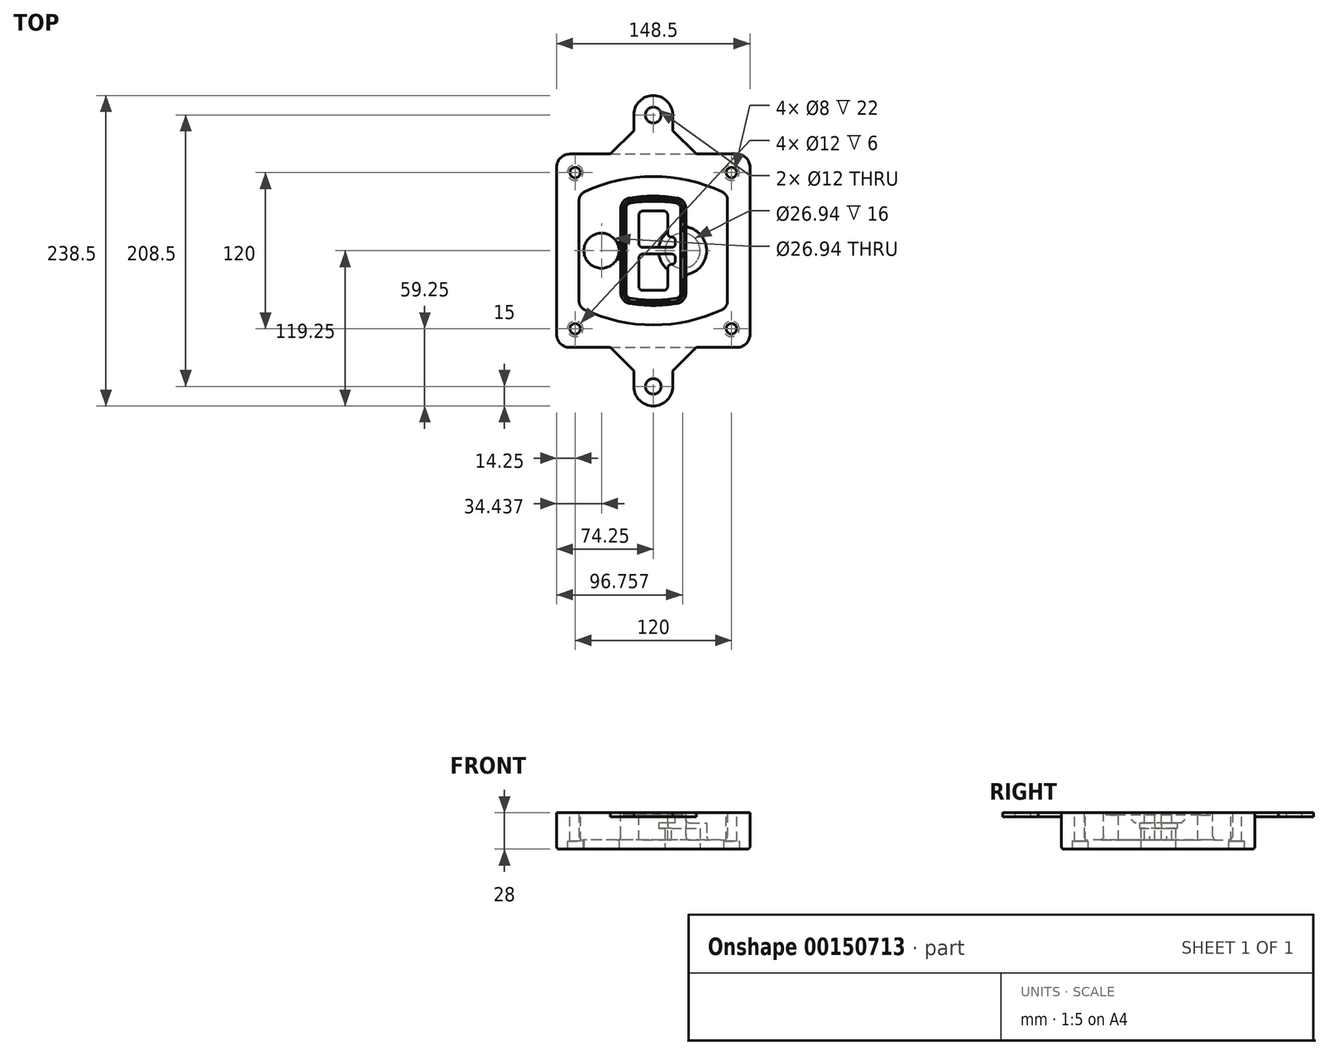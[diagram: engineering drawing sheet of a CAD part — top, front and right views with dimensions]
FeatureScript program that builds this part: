
annotation { "Feature Type Name" : "Feature", "Feature Type Description" : "" }
export const myFeature = defineFeature(function(context is Context, id is Id, definition is map)
    precondition{}
    {
        {
            var Q0;
            Q0=qCreatedBy(makeId("Top.planeOp"),FACE);
            var sketch = newSketch(context, id + "F0", { "sketchPlane" : qUnion([Q0])});
            skPoint(sketch, "E0.rect.middle", {"position": v(0, 0) * mm});
            skLineSegment(sketch, "E1.bottom", {"start": v(-64.25, -74.25) * mm, "end": v(64.25, -74.25) * mm});
            skLineSegment(sketch, "E1.top", {"start": v(-64.25, 74.25) * mm, "end": v(64.25, 74.25) * mm});
            skLineSegment(sketch, "E1.left", {"start": v(-74.25, -64.25) * mm, "end": v(-74.25, 64.25) * mm});
            skLineSegment(sketch, "E1.right", {"start": v(74.25, -64.25) * mm, "end": v(74.25, 64.25) * mm});
            skLineSegment(sketch, "E2", {"start": v(-74.25, 74.25) * mm, "end": v(74.25, -74.25) * mm, "construction": true});
            skLineSegment(sketch, "E3", {"start": v(74.25, 74.25) * mm, "end": v(-74.25, -74.25) * mm, "construction": true});
            skCircle(sketch, "E4", {"center": v(-60, 60) * mm, "radius": 4 * mm});
            skCircle(sketch, "E5", {"center": v(60, 60) * mm, "radius": 4 * mm});
            skCircle(sketch, "E6", {"center": v(60, -60) * mm, "radius": 4 * mm});
            skCircle(sketch, "E7", {"center": v(-60, -60) * mm, "radius": 4 * mm});
            skLineSegment(sketch, "E8", {"start": v(-60, 60) * mm, "end": v(60, 60) * mm, "construction": true});
            skLineSegment(sketch, "E9", {"start": v(60, 60) * mm, "end": v(60, -60) * mm, "construction": true});
            skLineSegment(sketch, "E10", {"start": v(60, -60) * mm, "end": v(-60, -60) * mm, "construction": true});
            skLineSegment(sketch, "E11", {"start": v(-60, -60) * mm, "end": v(-60, 60) * mm, "construction": true});
            skLineSegment(sketch, "E12", {"start": v(-60, 38.83) * mm, "end": v(-60, -38.83) * mm});
            skLineSegment(sketch, "E13", {"start": v(60, 38.83) * mm, "end": v(60, -38.83) * mm});
            skArc(sketch, "E14", {"start": v(54.26, 47.88) * mm, "mid": v(0, 60) * mm, "end": v(-54.26, 47.88) * mm});
            skArc(sketch, "E15", {"start": v(-54.26, -47.88) * mm, "mid": v(0, -60) * mm, "end": v(54.26, -47.88) * mm});
            skLineSegment(sketch, "E16", {"start": v(-60, 0) * mm, "end": v(60, 0) * mm, "construction": true});
            skPoint(sketch, "E17.visualSharp", {"position": v(-60, -45) * mm});
            skArc(sketch, "E17.filletArc", {"start": v(-60, -38.83) * mm, "mid": v(-58.44, -44.2) * mm, "end": v(-54.26, -47.88) * mm});
            skPoint(sketch, "E18.visualSharp", {"position": v(-60, 45) * mm});
            skArc(sketch, "E18.filletArc", {"start": v(-54.26, 47.88) * mm, "mid": v(-58.44, 44.2) * mm, "end": v(-60, 38.83) * mm});
            skPoint(sketch, "E19.visualSharp", {"position": v(60, 45) * mm});
            skArc(sketch, "E19.filletArc", {"start": v(60, 38.83) * mm, "mid": v(58.44, 44.2) * mm, "end": v(54.26, 47.88) * mm});
            skPoint(sketch, "E20.visualSharp", {"position": v(60, -45) * mm});
            skArc(sketch, "E20.filletArc", {"start": v(54.26, -47.88) * mm, "mid": v(58.44, -44.2) * mm, "end": v(60, -38.83) * mm});
            skPoint(sketch, "E21.visualSharp", {"position": v(-74.25, 74.25) * mm});
            skArc(sketch, "E21.filletArc", {"start": v(-64.25, 74.25) * mm, "mid": v(-71.32, 71.32) * mm, "end": v(-74.25, 64.25) * mm});
            skPoint(sketch, "E22.visualSharp", {"position": v(74.25, 74.25) * mm});
            skArc(sketch, "E22.filletArc", {"start": v(74.25, 64.25) * mm, "mid": v(71.32, 71.32) * mm, "end": v(64.25, 74.25) * mm});
            skPoint(sketch, "E23.visualSharp", {"position": v(74.25, -74.25) * mm});
            skArc(sketch, "E23.filletArc", {"start": v(64.25, -74.25) * mm, "mid": v(71.32, -71.32) * mm, "end": v(74.25, -64.25) * mm});
            skPoint(sketch, "E24.visualSharp", {"position": v(-74.25, -74.25) * mm});
            skArc(sketch, "E24.filletArc", {"start": v(-74.25, -64.25) * mm, "mid": v(-71.32, -71.32) * mm, "end": v(-64.25, -74.25) * mm});
            skArc(sketch, "E25.0", {"start": v(57, 38.83) * mm, "mid": v(55.9, 42.58) * mm, "end": v(52.98, 45.17) * mm});
            skLineSegment(sketch, "E25.1", {"start": v(57, 38.83) * mm, "end": v(57, -38.83) * mm});
            skArc(sketch, "E25.2", {"start": v(52.98, -45.17) * mm, "mid": v(55.9, -42.58) * mm, "end": v(57, -38.83) * mm});
            skArc(sketch, "E25.3", {"start": v(-52.98, -45.17) * mm, "mid": v(0, -57) * mm, "end": v(52.98, -45.17) * mm});
            skArc(sketch, "E25.4", {"start": v(-57, -38.83) * mm, "mid": v(-55.9, -42.58) * mm, "end": v(-52.98, -45.17) * mm});
            skArc(sketch, "E25.5", {"start": v(52.98, 45.17) * mm, "mid": v(0, 57) * mm, "end": v(-52.98, 45.17) * mm});
            skLineSegment(sketch, "E25.6", {"start": v(-57, 38.83) * mm, "end": v(-57, -38.83) * mm});
            skArc(sketch, "E25.7", {"start": v(-52.98, 45.17) * mm, "mid": v(-55.9, 42.58) * mm, "end": v(-57, 38.83) * mm});
            skArc(sketch, "E26.0", {"start": v(-55.96, 51.5) * mm, "mid": v(-61.82, 46.33) * mm, "end": v(-64, 38.83) * mm});
            skArc(sketch, "E26.1", {"start": v(55.96, 51.5) * mm, "mid": v(0, 64) * mm, "end": v(-55.96, 51.5) * mm});
            skArc(sketch, "E26.2", {"start": v(64, 38.83) * mm, "mid": v(61.82, 46.33) * mm, "end": v(55.96, 51.5) * mm});
            skLineSegment(sketch, "E26.3", {"start": v(64, 38.83) * mm, "end": v(64, -38.83) * mm});
            skArc(sketch, "E26.4", {"start": v(55.96, -51.5) * mm, "mid": v(61.82, -46.33) * mm, "end": v(64, -38.83) * mm});
            skLineSegment(sketch, "E26.5", {"start": v(-64, 38.83) * mm, "end": v(-64, -38.83) * mm});
            skArc(sketch, "E26.6", {"start": v(-55.96, -51.5) * mm, "mid": v(0, -64) * mm, "end": v(55.96, -51.5) * mm});
            skArc(sketch, "E26.7", {"start": v(-64, -38.83) * mm, "mid": v(-61.82, -46.33) * mm, "end": v(-55.96, -51.5) * mm});
            skSolve(sketch);
        }
        {
            var Q0;
            Q0=makeQuery(id+"F0.imprint","IMPRINT",FACE,{"disambiguationData":[TD([[makeQuery(id+"F0.imprint","IMPRINT",EDGE,{"derivedFrom":sQuery(id+"F0.wireOp",EDGE,"E1.bottom")}),1.0]])]});
            var Q1;
            Q1=makeQuery(id+"F0.imprint","IMPRINT",FACE,{"disambiguationData":[TD([[makeQuery(id+"F0.imprint","IMPRINT",EDGE,{"derivedFrom":sQuery(id+"F0.wireOp",EDGE,"E12")}),1.0]])]});
            var Q2;
            Q2=makeQuery(id+"F0.imprint","IMPRINT",FACE,{"disambiguationData":[TD([[makeQuery(id+"F0.imprint","IMPRINT",EDGE,{"derivedFrom":sQuery(id+"F0.wireOp",EDGE,"E25.0")}),1.0]])]});
            var Q3;
            Q3=makeQuery(id+"F0.imprint","IMPRINT",FACE,{"disambiguationData":[TD([[makeQuery(id+"F0.imprint","IMPRINT",EDGE,{"derivedFrom":sQuery(id+"F0.wireOp",EDGE,"E12")}),-1.0]])]});
            extrude(context, id + "F1", {"entities" : qUnion([Q0, Q1, Q2, Q3]), "oppositeDirection" : true, "depth" : 25 * mm});
        }
        {
            var Q0;
            Q0=makeQuery(id+"F0.imprint","IMPRINT",FACE,{"disambiguationData":[TD([[makeQuery(id+"F0.imprint","IMPRINT",EDGE,{"derivedFrom":sQuery(id+"F0.wireOp",EDGE,"E12")}),1.0]])]});
            extrude(context, id + "F2", {"entities" : qUnion([Q0]), "operationType" : NewBodyOperationType.ADD, "depth" : 3 * mm});
        }
        {
            var Q0;
            Q0=makeQuery(id+"F0.imprint","IMPRINT",FACE,{"disambiguationData":[TD([[makeQuery(id+"F0.imprint","IMPRINT",EDGE,{"derivedFrom":sQuery(id+"F0.wireOp",EDGE,"E25.0")}),1.0]])]});
            extrude(context, id + "F3", {"entities" : qUnion([Q0]), "operationType" : NewBodyOperationType.REMOVE, "oppositeDirection" : true, "depth" : 18 * mm});
        }
        {
            var Q0;
            Q0=makeQuery(id+"F2.opExtrude","CAP_FACE",FACE,{"disambiguationData":[OSD([sQuery(id+"F0.wireOp",EDGE,"E12"),sQuery(id+"F0.wireOp",EDGE,"E13"),sQuery(id+"F0.wireOp",EDGE,"E14"),sQuery(id+"F0.wireOp",EDGE,"E15"),sQuery(id+"F0.wireOp",EDGE,"E17.filletArc"),sQuery(id+"F0.wireOp",EDGE,"E18.filletArc"),sQuery(id+"F0.wireOp",EDGE,"E19.filletArc"),sQuery(id+"F0.wireOp",EDGE,"E20.filletArc"),sQuery(id+"F0.wireOp",EDGE,"E25.0"),sQuery(id+"F0.wireOp",EDGE,"E25.1"),sQuery(id+"F0.wireOp",EDGE,"E25.2"),sQuery(id+"F0.wireOp",EDGE,"E25.3"),sQuery(id+"F0.wireOp",EDGE,"E25.4"),sQuery(id+"F0.wireOp",EDGE,"E25.5"),sQuery(id+"F0.wireOp",EDGE,"E25.6"),sQuery(id+"F0.wireOp",EDGE,"E25.7")])],"isStart":false});
            var sketch = newSketch(context, id + "F4", { "sketchPlane" : qUnion([Q0])});
            skArc(sketch, "E27.0", {"start": v(-18.34, -40.45) * mm, "mid": v(0, -42) * mm, "end": v(18.34, -40.45) * mm});
            skArc(sketch, "E28.0", {"start": v(18.34, 40.45) * mm, "mid": v(0, 42) * mm, "end": v(-18.34, 40.45) * mm});
            skLineSegment(sketch, "E29", {"start": v(-25, 32.57) * mm, "end": v(-25, -32.57) * mm});
            skLineSegment(sketch, "E30", {"start": v(25, 32.57) * mm, "end": v(25, -32.57) * mm});
            skLineSegment(sketch, "E31", {"start": v(-25, 39.1) * mm, "end": v(25, 39.1) * mm, "construction": true});
            skLineSegment(sketch, "E32", {"start": v(-25, -39.1) * mm, "end": v(25, -39.1) * mm, "construction": true});
            skPoint(sketch, "E33.visualSharp", {"position": v(-25, 39.1) * mm});
            skArc(sketch, "E33.filletArc", {"start": v(-18.34, 40.45) * mm, "mid": v(-23.11, 37.73) * mm, "end": v(-25, 32.57) * mm});
            skPoint(sketch, "E34.visualSharp", {"position": v(25, 39.1) * mm});
            skArc(sketch, "E34.filletArc", {"start": v(25, 32.57) * mm, "mid": v(23.11, 37.73) * mm, "end": v(18.34, 40.45) * mm});
            skPoint(sketch, "E35.visualSharp", {"position": v(25, -39.1) * mm});
            skArc(sketch, "E35.filletArc", {"start": v(18.34, -40.45) * mm, "mid": v(23.11, -37.73) * mm, "end": v(25, -32.57) * mm});
            skPoint(sketch, "E36.visualSharp", {"position": v(-25, -39.1) * mm});
            skArc(sketch, "E36.filletArc", {"start": v(-25, -32.57) * mm, "mid": v(-23.11, -37.73) * mm, "end": v(-18.34, -40.45) * mm});
            skArc(sketch, "E37.0", {"start": v(52.98, 45.17) * mm, "mid": v(0, 57) * mm, "end": v(-52.98, 45.17) * mm});
            skArc(sketch, "E37.1", {"start": v(-52.98, 45.17) * mm, "mid": v(-55.9, 42.58) * mm, "end": v(-57, 38.83) * mm});
            skLineSegment(sketch, "E37.2", {"start": v(-57, 38.83) * mm, "end": v(-57, -38.83) * mm});
            skArc(sketch, "E37.3", {"start": v(-57, -38.83) * mm, "mid": v(-55.9, -42.58) * mm, "end": v(-52.98, -45.17) * mm});
            skArc(sketch, "E37.4", {"start": v(-52.98, -45.17) * mm, "mid": v(0, -57) * mm, "end": v(52.98, -45.17) * mm});
            skArc(sketch, "E37.5", {"start": v(52.98, -45.17) * mm, "mid": v(55.9, -42.58) * mm, "end": v(57, -38.83) * mm});
            skLineSegment(sketch, "E37.6", {"start": v(57, 38.83) * mm, "end": v(57, -38.83) * mm});
            skArc(sketch, "E37.7", {"start": v(57, 38.83) * mm, "mid": v(55.9, 42.58) * mm, "end": v(52.98, 45.17) * mm});
            skLineSegment(sketch, "E38.0", {"start": v(23, 32.57) * mm, "end": v(23, -32.57) * mm});
            skArc(sketch, "E38.1", {"start": v(18, -38.48) * mm, "mid": v(21.58, -36.44) * mm, "end": v(23, -32.57) * mm});
            skArc(sketch, "E38.2", {"start": v(-18, -38.48) * mm, "mid": v(0, -40) * mm, "end": v(18, -38.48) * mm});
            skArc(sketch, "E38.3", {"start": v(-23, -32.57) * mm, "mid": v(-21.58, -36.44) * mm, "end": v(-18, -38.48) * mm});
            skLineSegment(sketch, "E38.4", {"start": v(-23, 32.57) * mm, "end": v(-23, -32.57) * mm});
            skArc(sketch, "E38.5", {"start": v(23, 32.57) * mm, "mid": v(21.58, 36.44) * mm, "end": v(18, 38.48) * mm});
            skArc(sketch, "E38.6", {"start": v(-18, 38.48) * mm, "mid": v(-21.58, 36.44) * mm, "end": v(-23, 32.57) * mm});
            skArc(sketch, "E38.7", {"start": v(18, 38.48) * mm, "mid": v(0, 40) * mm, "end": v(-18, 38.48) * mm});
            skArc(sketch, "E39.0", {"start": v(21, 32.57) * mm, "mid": v(20.06, 35.15) * mm, "end": v(17.67, 36.5) * mm});
            skLineSegment(sketch, "E39.1", {"start": v(21, 32.57) * mm, "end": v(21, -32.57) * mm});
            skArc(sketch, "E39.2", {"start": v(17.67, -36.5) * mm, "mid": v(20.06, -35.15) * mm, "end": v(21, -32.57) * mm});
            skArc(sketch, "E39.3", {"start": v(-17.67, -36.5) * mm, "mid": v(0, -38) * mm, "end": v(17.67, -36.5) * mm});
            skArc(sketch, "E39.4", {"start": v(-21, -32.57) * mm, "mid": v(-20.06, -35.15) * mm, "end": v(-17.67, -36.5) * mm});
            skArc(sketch, "E39.5", {"start": v(17.67, 36.5) * mm, "mid": v(0, 38) * mm, "end": v(-17.67, 36.5) * mm});
            skLineSegment(sketch, "E39.6", {"start": v(-21, 32.57) * mm, "end": v(-21, -32.57) * mm});
            skArc(sketch, "E39.7", {"start": v(-17.67, 36.5) * mm, "mid": v(-20.06, 35.15) * mm, "end": v(-21, 32.57) * mm});
            skLineSegment(sketch, "E40", {"start": v(-25, 0) * mm, "end": v(25, 0) * mm, "construction": true});
            skLineSegment(sketch, "E41", {"start": v(-11, 5.5) * mm, "end": v(-11, 27.5) * mm});
            skLineSegment(sketch, "E42", {"start": v(-8, 30.5) * mm, "end": v(8, 30.5) * mm});
            skLineSegment(sketch, "E43", {"start": v(11, 27.5) * mm, "end": v(11, 13.5) * mm});
            skLineSegment(sketch, "E44", {"start": v(14, 10.5) * mm, "end": v(14, 10.5) * mm});
            skLineSegment(sketch, "E45", {"start": v(17, 7.5) * mm, "end": v(17, 5.5) * mm});
            skLineSegment(sketch, "E46", {"start": v(14, 2.5) * mm, "end": v(-8, 2.5) * mm});
            skPoint(sketch, "E47.visualSharp", {"position": v(-11, 30.5) * mm});
            skArc(sketch, "E47.filletArc", {"start": v(-8, 30.5) * mm, "mid": v(-10.12, 29.62) * mm, "end": v(-11, 27.5) * mm});
            skPoint(sketch, "E48.visualSharp", {"position": v(11, 30.5) * mm});
            skArc(sketch, "E48.filletArc", {"start": v(11, 27.5) * mm, "mid": v(10.12, 29.62) * mm, "end": v(8, 30.5) * mm});
            skPoint(sketch, "E49.visualSharp", {"position": v(11, 10.5) * mm});
            skArc(sketch, "E49.filletArc", {"start": v(11, 13.5) * mm, "mid": v(11.88, 11.38) * mm, "end": v(14, 10.5) * mm});
            skPoint(sketch, "E50.visualSharp", {"position": v(17, 10.5) * mm});
            skArc(sketch, "E50.filletArc", {"start": v(17, 7.5) * mm, "mid": v(16.12, 9.62) * mm, "end": v(14, 10.5) * mm});
            skPoint(sketch, "E51.visualSharp", {"position": v(17, 2.5) * mm});
            skArc(sketch, "E51.filletArc", {"start": v(14, 2.5) * mm, "mid": v(16.12, 3.38) * mm, "end": v(17, 5.5) * mm});
            skPoint(sketch, "E52.visualSharp", {"position": v(-11, 2.5) * mm});
            skArc(sketch, "E52.filletArc", {"start": v(-11, 5.5) * mm, "mid": v(-10.12, 3.38) * mm, "end": v(-8, 2.5) * mm});
            skLineSegment(sketch, "E53.0.MirrorCS", {"start": v(14, -2.5) * mm, "end": v(-8, -2.5) * mm});
            skArc(sketch, "E54.0.MirrorCS", {"start": v(-11, -5.5) * mm, "mid": v(-10.12, -3.38) * mm, "end": v(-8, -2.5) * mm});
            skLineSegment(sketch, "E55.0.MirrorCS", {"start": v(-11, -5.5) * mm, "end": v(-11, -27.5) * mm});
            skArc(sketch, "E56.0.MirrorCS", {"start": v(-8, -30.5) * mm, "mid": v(-10.12, -29.62) * mm, "end": v(-11, -27.5) * mm});
            skLineSegment(sketch, "E57.0.MirrorCS", {"start": v(-8, -30.5) * mm, "end": v(8, -30.5) * mm});
            skArc(sketch, "E58.0.MirrorCS", {"start": v(11, -27.5) * mm, "mid": v(10.12, -29.62) * mm, "end": v(8, -30.5) * mm});
            skLineSegment(sketch, "E59.0.MirrorCS", {"start": v(11, -27.5) * mm, "end": v(11, -13.5) * mm});
            skArc(sketch, "E60.0.MirrorCS", {"start": v(11, -13.5) * mm, "mid": v(11.88, -11.38) * mm, "end": v(14, -10.5) * mm});
            skArc(sketch, "E61.0.MirrorCS", {"start": v(17, -7.5) * mm, "mid": v(16.12, -9.62) * mm, "end": v(14, -10.5) * mm});
            skLineSegment(sketch, "E62.0.MirrorCS", {"start": v(17, -7.5) * mm, "end": v(17, -5.5) * mm});
            skArc(sketch, "E63.0.MirrorCS", {"start": v(14, -2.5) * mm, "mid": v(16.12, -3.38) * mm, "end": v(17, -5.5) * mm});
            skSolve(sketch);
        }
        {
            var Q0;
            Q0=makeQuery(id+"F4.imprint","IMPRINT",FACE,{"disambiguationData":[TD([[makeQuery(id+"F4.imprint","IMPRINT",EDGE,{"derivedFrom":sQuery(id+"F4.wireOp",EDGE,"E27.0")}),1.0]])]});
            var Q1;
            Q1=makeQuery(id+"F4.imprint","IMPRINT",FACE,{"disambiguationData":[TD([[makeQuery(id+"F4.imprint","IMPRINT",EDGE,{"derivedFrom":sQuery(id+"F4.wireOp",EDGE,"E38.0")}),-1.0]])]});
            var Q2;
            Q2=makeQuery(id+"F4.imprint","IMPRINT",FACE,{"disambiguationData":[TD([[makeQuery(id+"F4.imprint","IMPRINT",EDGE,{"derivedFrom":sQuery(id+"F4.wireOp",EDGE,"E39.0")}),1.0]])]});
            extrude(context, id + "F5", {"entities" : qUnion([Q0, Q1, Q2]), "operationType" : NewBodyOperationType.ADD, "endBound" : BoundingType.UP_TO_NEXT, "oppositeDirection" : true, "depth" : 25 * mm});
        }
        {
            var Q0;
            Q0=makeQuery(id+"F4.imprint","IMPRINT",FACE,{"disambiguationData":[TD([[makeQuery(id+"F4.imprint","IMPRINT",EDGE,{"derivedFrom":sQuery(id+"F4.wireOp",EDGE,"E38.0")}),-1.0]])]});
            extrude(context, id + "F6", {"entities" : qUnion([Q0]), "operationType" : NewBodyOperationType.REMOVE, "oppositeDirection" : true, "depth" : 2 * mm});
        }
        {
            var Q0;
            Q0=makeQuery(id+"F1.opExtrude","CAP_FACE",FACE,{"disambiguationData":[OSD([sQuery(id+"F0.wireOp",EDGE,"E1.bottom"),sQuery(id+"F0.wireOp",EDGE,"E1.top"),sQuery(id+"F0.wireOp",EDGE,"E1.left"),sQuery(id+"F0.wireOp",EDGE,"E1.right"),sQuery(id+"F0.wireOp",EDGE,"E4"),sQuery(id+"F0.wireOp",EDGE,"E5"),sQuery(id+"F0.wireOp",EDGE,"E6"),sQuery(id+"F0.wireOp",EDGE,"E7"),sQuery(id+"F0.wireOp",EDGE,"E21.filletArc"),sQuery(id+"F0.wireOp",EDGE,"E22.filletArc"),sQuery(id+"F0.wireOp",EDGE,"E23.filletArc"),sQuery(id+"F0.wireOp",EDGE,"E24.filletArc")])],"isStart":false});
            var sketch = newSketch(context, id + "F7", { "sketchPlane" : qUnion([Q0])});
            skCircle(sketch, "E64", {"center": v(22.5, 0) * mm, "radius": 13.47 * mm});
            skCircle(sketch, "E65", {"center": v(-39.81, 0) * mm, "radius": 13.47 * mm});
            skLineSegment(sketch, "E66", {"start": v(74.25, 0) * mm, "end": v(-74.25, 0) * mm});
            skCircle(sketch, "E67", {"center": v(22.5, 0) * mm, "radius": 18.47 * mm});
            skCircle(sketch, "E68", {"center": v(60, -60) * mm, "radius": 6 * mm});
            skCircle(sketch, "E69", {"center": v(-60, -60) * mm, "radius": 6 * mm});
            skCircle(sketch, "E70", {"center": v(-60, 60) * mm, "radius": 6 * mm});
            skCircle(sketch, "E71", {"center": v(60, 60) * mm, "radius": 6 * mm});
            skSolve(sketch);
        }
        {
            var Q0;
            {var subQ1=sQuery(id+"F7.wireOp",EDGE,"E66");var subQ4=sQuery(id+"F7.wireOp",EDGE,"E64");var subQ6=makeQuery(id+"F7.imprint","INTERSECT",VERTEX,{"disambiguationData":[OD(0.0)],"derivedFrom":[subQ4,subQ1]});Q0=makeQuery(id+"F7.imprint","IMPRINT",FACE,{"disambiguationData":[TD([[makeQuery(id+"F7.imprint","IMPRINT",EDGE,{"disambiguationData":[TD([[subQ6,-1.0]])],"derivedFrom":subQ4}),-1.0]])]});}
            var Q1;
            {var subQ0=sQuery(id+"F7.wireOp",EDGE,"E66");var subQ1=sQuery(id+"F7.wireOp",EDGE,"E64");var subQ3=makeQuery(id+"F7.imprint","INTERSECT",VERTEX,{"disambiguationData":[OD(0.0)],"derivedFrom":[subQ1,subQ0]});Q1=makeQuery(id+"F7.imprint","IMPRINT",FACE,{"disambiguationData":[TD([[makeQuery(id+"F7.imprint","IMPRINT",EDGE,{"disambiguationData":[TD([[subQ3,-1.0]])],"derivedFrom":subQ1}),1.0]])]});}
            var Q2;
            {var subQ0=sQuery(id+"F7.wireOp",EDGE,"E66");var subQ1=sQuery(id+"F7.wireOp",EDGE,"E64");var subQ3=makeQuery(id+"F7.imprint","INTERSECT",VERTEX,{"disambiguationData":[OD(0.0)],"derivedFrom":[subQ1,subQ0]});Q2=makeQuery(id+"F7.imprint","IMPRINT",FACE,{"disambiguationData":[TD([[makeQuery(id+"F7.imprint","IMPRINT",EDGE,{"disambiguationData":[TD([[subQ3,1.0]])],"derivedFrom":subQ1}),1.0]])]});}
            var Q3;
            {var subQ1=sQuery(id+"F7.wireOp",EDGE,"E66");var subQ4=sQuery(id+"F7.wireOp",EDGE,"E64");var subQ6=makeQuery(id+"F7.imprint","INTERSECT",VERTEX,{"disambiguationData":[OD(0.0)],"derivedFrom":[subQ4,subQ1]});Q3=makeQuery(id+"F7.imprint","IMPRINT",FACE,{"disambiguationData":[TD([[makeQuery(id+"F7.imprint","IMPRINT",EDGE,{"disambiguationData":[TD([[subQ6,1.0]])],"derivedFrom":subQ4}),-1.0]])]});}
            extrude(context, id + "F8", {"entities" : qUnion([Q0, Q1, Q2, Q3]), "operationType" : NewBodyOperationType.ADD, "oppositeDirection" : true, "depth" : 20 * mm});
        }
        {
            var Q0;
            {var subQ0=sQuery(id+"F7.wireOp",EDGE,"E66");var subQ1=sQuery(id+"F7.wireOp",EDGE,"E64");var subQ3=makeQuery(id+"F7.imprint","INTERSECT",VERTEX,{"disambiguationData":[OD(0.0)],"derivedFrom":[subQ1,subQ0]});Q0=makeQuery(id+"F7.imprint","IMPRINT",FACE,{"disambiguationData":[TD([[makeQuery(id+"F7.imprint","IMPRINT",EDGE,{"disambiguationData":[TD([[subQ3,-1.0]])],"derivedFrom":subQ1}),1.0]])]});}
            var Q1;
            {var subQ0=sQuery(id+"F7.wireOp",EDGE,"E66");var subQ1=sQuery(id+"F7.wireOp",EDGE,"E64");var subQ3=makeQuery(id+"F7.imprint","INTERSECT",VERTEX,{"disambiguationData":[OD(0.0)],"derivedFrom":[subQ1,subQ0]});Q1=makeQuery(id+"F7.imprint","IMPRINT",FACE,{"disambiguationData":[TD([[makeQuery(id+"F7.imprint","IMPRINT",EDGE,{"disambiguationData":[TD([[subQ3,1.0]])],"derivedFrom":subQ1}),1.0]])]});}
            extrude(context, id + "F9", {"entities" : qUnion([Q0, Q1]), "operationType" : NewBodyOperationType.REMOVE, "oppositeDirection" : true, "depth" : 16 * mm});
        }
        {
            var Q0;
            {var subQ0=sQuery(id+"F7.wireOp",EDGE,"E66");var subQ1=sQuery(id+"F7.wireOp",EDGE,"E65");var subQ3=makeQuery(id+"F7.imprint","INTERSECT",VERTEX,{"disambiguationData":[OD(0.0)],"derivedFrom":[subQ1,subQ0]});Q0=makeQuery(id+"F7.imprint","IMPRINT",FACE,{"disambiguationData":[TD([[makeQuery(id+"F7.imprint","IMPRINT",EDGE,{"disambiguationData":[TD([[subQ3,-1.0]])],"derivedFrom":subQ1}),1.0]])]});}
            var Q1;
            {var subQ0=sQuery(id+"F7.wireOp",EDGE,"E66");var subQ1=sQuery(id+"F7.wireOp",EDGE,"E65");var subQ3=makeQuery(id+"F7.imprint","INTERSECT",VERTEX,{"disambiguationData":[OD(0.0)],"derivedFrom":[subQ1,subQ0]});Q1=makeQuery(id+"F7.imprint","IMPRINT",FACE,{"disambiguationData":[TD([[makeQuery(id+"F7.imprint","IMPRINT",EDGE,{"disambiguationData":[TD([[subQ3,1.0]])],"derivedFrom":subQ1}),1.0]])]});}
            extrude(context, id + "F10", {"entities" : qUnion([Q0, Q1]), "operationType" : NewBodyOperationType.REMOVE, "oppositeDirection" : true, "depth" : 25 * mm});
        }
        {
            var Q0;
            Q0=makeQuery(id+"F7.imprint","IMPRINT",FACE,{"disambiguationData":[TD([[makeQuery(id+"F7.imprint","IMPRINT",EDGE,{"derivedFrom":sQuery(id+"F7.wireOp",EDGE,"E68")}),1.0]])]});
            var Q1;
            Q1=makeQuery(id+"F7.imprint","IMPRINT",FACE,{"disambiguationData":[TD([[makeQuery(id+"F7.imprint","IMPRINT",EDGE,{"derivedFrom":makeQuery(id+"F1.opExtrude","CAP_EDGE",EDGE,{"disambiguationData":[OSD([sQuery(id+"F0.wireOp",EDGE,"E5")])],"isStart":false})}),-1.0]])]});
            var Q2;
            Q2=makeQuery(id+"F7.imprint","IMPRINT",FACE,{"disambiguationData":[TD([[makeQuery(id+"F7.imprint","IMPRINT",EDGE,{"derivedFrom":sQuery(id+"F7.wireOp",EDGE,"E69")}),1.0]])]});
            var Q3;
            Q3=makeQuery(id+"F7.imprint","IMPRINT",FACE,{"disambiguationData":[TD([[makeQuery(id+"F7.imprint","IMPRINT",EDGE,{"derivedFrom":makeQuery(id+"F1.opExtrude","CAP_EDGE",EDGE,{"disambiguationData":[OSD([sQuery(id+"F0.wireOp",EDGE,"E4")])],"isStart":false})}),-1.0]])]});
            var Q4;
            Q4=makeQuery(id+"F7.imprint","IMPRINT",FACE,{"disambiguationData":[TD([[makeQuery(id+"F7.imprint","IMPRINT",EDGE,{"derivedFrom":sQuery(id+"F7.wireOp",EDGE,"E70")}),1.0]])]});
            var Q5;
            Q5=makeQuery(id+"F7.imprint","IMPRINT",FACE,{"disambiguationData":[TD([[makeQuery(id+"F7.imprint","IMPRINT",EDGE,{"derivedFrom":makeQuery(id+"F1.opExtrude","CAP_EDGE",EDGE,{"disambiguationData":[OSD([sQuery(id+"F0.wireOp",EDGE,"E7")])],"isStart":false})}),-1.0]])]});
            var Q6;
            Q6=makeQuery(id+"F7.imprint","IMPRINT",FACE,{"disambiguationData":[TD([[makeQuery(id+"F7.imprint","IMPRINT",EDGE,{"derivedFrom":sQuery(id+"F7.wireOp",EDGE,"E71")}),1.0]])]});
            var Q7;
            Q7=makeQuery(id+"F7.imprint","IMPRINT",FACE,{"disambiguationData":[TD([[makeQuery(id+"F7.imprint","IMPRINT",EDGE,{"derivedFrom":makeQuery(id+"F1.opExtrude","CAP_EDGE",EDGE,{"disambiguationData":[OSD([sQuery(id+"F0.wireOp",EDGE,"E6")])],"isStart":false})}),-1.0]])]});
            extrude(context, id + "F11", {"entities" : qUnion([Q0, Q1, Q2, Q3, Q4, Q5, Q6, Q7]), "operationType" : NewBodyOperationType.REMOVE, "oppositeDirection" : true, "depth" : 6 * mm});
        }
        {
            var Q0;
            Q0=makeQuery(id+"F9.boolean.opBoolean","COPY",FACE,{"derivedFrom":makeQuery(id+"F9.opExtrude","CAP_FACE",FACE,{"disambiguationData":[OSD([sQuery(id+"F7.wireOp",EDGE,"E64")])],"isStart":false})});
            var sketch = newSketch(context, id + "F12", { "sketchPlane" : qUnion([Q0])});
            skArc(sketch, "E72.0", {"start": v(11, 14.45) * mm, "mid": v(6.45, 9.13) * mm, "end": v(4.2, 2.5) * mm});
            skArc(sketch, "E72.1", {"start": v(4.2, -2.5) * mm, "mid": v(6.45, -9.13) * mm, "end": v(11, -14.45) * mm});
            skLineSegment(sketch, "E73", {"start": v(4.2, -2.5) * mm, "end": v(14, -2.5) * mm});
            skLineSegment(sketch, "E74.0", {"start": v(14, 2.5) * mm, "end": v(4.2, 2.5) * mm});
            skArc(sketch, "E74.1", {"start": v(14, 2.5) * mm, "mid": v(16.12, 3.38) * mm, "end": v(17, 5.5) * mm});
            skLineSegment(sketch, "E74.2", {"start": v(17, 7.5) * mm, "end": v(17, 5.5) * mm});
            skArc(sketch, "E74.3", {"start": v(17, 7.5) * mm, "mid": v(16.12, 9.62) * mm, "end": v(14, 10.5) * mm});
            skArc(sketch, "E74.4", {"start": v(11, 13.5) * mm, "mid": v(11.88, 11.38) * mm, "end": v(14, 10.5) * mm});
            skLineSegment(sketch, "E74.5", {"start": v(11, 14.45) * mm, "end": v(11, 13.5) * mm});
            skLineSegment(sketch, "E74.7", {"start": v(14, -2.5) * mm, "end": v(4.2, -2.5) * mm});
            skArc(sketch, "E74.8", {"start": v(14, -2.5) * mm, "mid": v(16.12, -3.38) * mm, "end": v(17, -5.5) * mm});
            skLineSegment(sketch, "E74.9", {"start": v(17, -7.5) * mm, "end": v(17, -5.5) * mm});
            skArc(sketch, "E74.10", {"start": v(17, -7.5) * mm, "mid": v(16.12, -9.62) * mm, "end": v(14, -10.5) * mm});
            skArc(sketch, "E74.11", {"start": v(11, -13.5) * mm, "mid": v(11.88, -11.38) * mm, "end": v(14, -10.5) * mm});
            skLineSegment(sketch, "E74.12", {"start": v(11, -14.45) * mm, "end": v(11, -13.5) * mm});
            skPoint(sketch, "E75.orphan", {"position": v(11, -27.5) * mm});
            skPoint(sketch, "E76.orphan", {"position": v(-8, -2.5) * mm});
            skPoint(sketch, "E77.orphan", {"position": v(-8, 2.5) * mm});
            skPoint(sketch, "E78.orphan", {"position": v(11, 27.5) * mm});
            skSolve(sketch);
        }
        {
            var Q0;
            {var subQ7=sQuery(id+"F12.wireOp",EDGE,"E72.0");var subQ14=sQuery(id+"F12.wireOp",EDGE,"E72.1");var subQ16=sQuery(id+"F12.wireOp",EDGE,"E74.1");var subQ18=sQuery(id+"F12.wireOp",EDGE,"E74.8");Q0=qUnion([makeQuery(id+"F12.imprint","IMPRINT",FACE,{"disambiguationData":[TD([[makeQuery(id+"F12.imprint","IMPRINT",EDGE,{"derivedFrom":subQ7}),1.0]])]}),makeQuery(id+"F12.imprint","IMPRINT",FACE,{"disambiguationData":[TD([[makeQuery(id+"F12.imprint","IMPRINT",EDGE,{"derivedFrom":subQ14}),1.0]])]}),makeQuery(id+"F12.imprint","IMPRINT",FACE,{"disambiguationData":[TD([[makeQuery(id+"F12.imprint","IMPRINT",EDGE,{"derivedFrom":subQ16}),1.0]])]}),makeQuery(id+"F12.imprint","IMPRINT",FACE,{"disambiguationData":[TD([[makeQuery(id+"F12.imprint","IMPRINT",EDGE,{"derivedFrom":subQ18}),-1.0]])]})]);}
            var Q1;
            Q1=makeQuery(id+"F5.boolean.opBoolean","SPLIT",FACE,{"disambiguationData":[TD([makeQuery(id+"F5.opExtrude","SWEPT_FACE",FACE,{"disambiguationData":[OSD([sQuery(id+"F4.wireOp",EDGE,"E41")])]})])],"derivedFrom":makeQuery(id+"F3.boolean.opBoolean","COPY",FACE,{"derivedFrom":makeQuery(id+"F3.opExtrude","CAP_FACE",FACE,{"disambiguationData":[OSD([sQuery(id+"F0.wireOp",EDGE,"E25.0"),sQuery(id+"F0.wireOp",EDGE,"E25.1"),sQuery(id+"F0.wireOp",EDGE,"E25.2"),sQuery(id+"F0.wireOp",EDGE,"E25.3"),sQuery(id+"F0.wireOp",EDGE,"E25.4"),sQuery(id+"F0.wireOp",EDGE,"E25.5"),sQuery(id+"F0.wireOp",EDGE,"E25.6"),sQuery(id+"F0.wireOp",EDGE,"E25.7")])],"isStart":false})})});
            extrude(context, id + "F13", {"entities" : qUnion([Q0]), "operationType" : NewBodyOperationType.REMOVE, "endBound" : BoundingType.UP_TO_SURFACE, "endBoundEntityFace" : qUnion([Q1]), "depth" : 25 * mm});
        }
        {
            var Q0;
            Q0=makeQuery(id+"F3.boolean.opBoolean","COPY",EDGE,{"derivedFrom":makeQuery(id+"F3.opExtrude","CAP_EDGE",EDGE,{"disambiguationData":[OSD([sQuery(id+"F0.wireOp",EDGE,"E25.6")])],"isStart":false})});
            var Q1;
            Q1=makeQuery(id+"F8.boolean.opBoolean","INTERSECT",EDGE,{"derivedFrom":[makeQuery(id+"F5.opExtrude","SWEPT_FACE",FACE,{"disambiguationData":[OSD([sQuery(id+"F4.wireOp",EDGE,"E30")])]}),makeQuery(id+"F8.opExtrude","CAP_FACE",FACE,{"disambiguationData":[OSD([sQuery(id+"F7.wireOp",EDGE,"E67")])],"isStart":false})]});
            var Q2;
            Q2=makeQuery(id+"F8.boolean.opBoolean","INTERSECT",EDGE,{"disambiguationData":[OD(1.0)],"derivedFrom":[makeQuery(id+"F5.opExtrude","SWEPT_FACE",FACE,{"disambiguationData":[OSD([sQuery(id+"F4.wireOp",EDGE,"E30")])]}),makeQuery(id+"F8.opExtrude","SWEPT_FACE",FACE,{"disambiguationData":[OSD([sQuery(id+"F7.wireOp",EDGE,"E67")])]})]});
            var Q3;
            {var subQ0=sQuery(id+"F4.wireOp",EDGE,"E30");Q3=makeQuery(id+"F8.boolean.opBoolean","SPLIT",EDGE,{"disambiguationData":[TD([makeQuery(id+"F5.opExtrude","SWEPT_FACE",FACE,{"disambiguationData":[OSD([sQuery(id+"F4.wireOp",EDGE,"E35.filletArc")])]})])],"derivedFrom":makeQuery(id+"F5.opExtrude","CAP_EDGE",EDGE,{"disambiguationData":[OSD([subQ0])],"isStart":false})});}
            var Q4;
            {var subQ0=sQuery(id+"F0.wireOp",EDGE,"E25.7");var subQ1=sQuery(id+"F0.wireOp",EDGE,"E25.1");var subQ2=sQuery(id+"F0.wireOp",EDGE,"E25.6");var subQ3=sQuery(id+"F0.wireOp",EDGE,"E25.5");var subQ4=sQuery(id+"F0.wireOp",EDGE,"E25.4");var subQ5=sQuery(id+"F0.wireOp",EDGE,"E25.0");var subQ6=sQuery(id+"F0.wireOp",EDGE,"E25.2");var subQ7=sQuery(id+"F0.wireOp",EDGE,"E25.3");Q4=makeQuery(id+"F8.boolean.opBoolean","INTERSECT",EDGE,{"derivedFrom":[makeQuery(id+"F5.boolean.opBoolean","SPLIT",FACE,{"disambiguationData":[TD([makeQuery(id+"F2.opExtrude","SWEPT_FACE",FACE,{"disambiguationData":[OSD([subQ5])]})])],"derivedFrom":makeQuery(id+"F3.boolean.opBoolean","COPY",FACE,{"derivedFrom":makeQuery(id+"F3.opExtrude","CAP_FACE",FACE,{"disambiguationData":[OSD([subQ5,subQ1,subQ6,subQ7,subQ4,subQ3,subQ2,subQ0])],"isStart":false})})}),makeQuery(id+"F8.opExtrude","SWEPT_FACE",FACE,{"disambiguationData":[OSD([sQuery(id+"F7.wireOp",EDGE,"E67")])]})]});}
            var Q5;
            Q5=makeQuery(id+"F8.boolean.opBoolean","INTERSECT",EDGE,{"disambiguationData":[OD(0.0)],"derivedFrom":[makeQuery(id+"F5.opExtrude","SWEPT_FACE",FACE,{"disambiguationData":[OSD([sQuery(id+"F4.wireOp",EDGE,"E30")])]}),makeQuery(id+"F8.opExtrude","SWEPT_FACE",FACE,{"disambiguationData":[OSD([sQuery(id+"F7.wireOp",EDGE,"E67")])]})]});
            fillet(context, id + "F14", {"entities" : qUnion([Q0, Q1, Q2, Q3, Q4, Q5]), "radius" : 3 * mm, "tangentPropagation" : true, "allowEdgeOverflow" : false});
        }
        {
            var Q0;
            Q0=makeQuery(id+"F1.opExtrude","CAP_EDGE",EDGE,{"disambiguationData":[OSD([sQuery(id+"F0.wireOp",EDGE,"E1.bottom")])],"isStart":false});
            fillet(context, id + "F15", {"entities" : qUnion([Q0]), "radius" : 2 * mm, "tangentPropagation" : true, "allowEdgeOverflow" : false});
        }
        {
            var Q0;
            {var subQ0=sQuery(id+"F0.wireOp",EDGE,"E22.filletArc");var subQ1=sQuery(id+"F0.wireOp",EDGE,"E7");var subQ2=sQuery(id+"F0.wireOp",EDGE,"E6");var subQ3=sQuery(id+"F0.wireOp",EDGE,"E5");var subQ4=sQuery(id+"F0.wireOp",EDGE,"E4");var subQ5=sQuery(id+"F0.wireOp",EDGE,"E1.bottom");var subQ6=sQuery(id+"F0.wireOp",EDGE,"E21.filletArc");var subQ7=sQuery(id+"F0.wireOp",EDGE,"E1.top");var subQ8=sQuery(id+"F0.wireOp",EDGE,"E1.left");var subQ9=sQuery(id+"F0.wireOp",EDGE,"E1.right");var subQ10=sQuery(id+"F0.wireOp",EDGE,"E23.filletArc");var subQ11=sQuery(id+"F0.wireOp",EDGE,"E24.filletArc");Q0=makeQuery(id+"F2.boolean.opBoolean","SPLIT",FACE,{"disambiguationData":[TD([makeQuery(id+"F1.opExtrude","SWEPT_FACE",FACE,{"disambiguationData":[OSD([subQ5])]})])],"derivedFrom":makeQuery(id+"F1.opExtrude","CAP_FACE",FACE,{"disambiguationData":[OSD([subQ5,subQ7,subQ8,subQ9,subQ4,subQ3,subQ2,subQ1,subQ6,subQ0,subQ10,subQ11])],"isStart":true})});}
            var sketch = newSketch(context, id + "F16", { "sketchPlane" : qUnion([Q0])});
            skLineSegment(sketch, "E79", {"start": v(0, 74.25) * mm, "end": v(0, 104.25) * mm, "construction": true});
            skCircle(sketch, "E80", {"center": v(0, 104.25) * mm, "radius": 6 * mm});
            skArc(sketch, "E81", {"start": v(15, 104.25) * mm, "mid": v(0, 119.25) * mm, "end": v(-15, 104.25) * mm});
            skLineSegment(sketch, "E82", {"start": v(-15, 104.25) * mm, "end": v(-15, 92.25) * mm});
            skLineSegment(sketch, "E83", {"start": v(15, 104.25) * mm, "end": v(15, 92.25) * mm});
            skLineSegment(sketch, "E84", {"start": v(15, 92.25) * mm, "end": v(33, 74.25) * mm});
            skLineSegment(sketch, "E85", {"start": v(-15, 92.25) * mm, "end": v(-33, 74.25) * mm});
            skLineSegment(sketch, "E86", {"start": v(-74.25, 0) * mm, "end": v(74.25, 0) * mm, "construction": true});
            skLineSegment(sketch, "E87.MirrorCS", {"start": v(-15, -104.25) * mm, "end": v(-15, -92.25) * mm});
            skLineSegment(sketch, "E88.MirrorCS", {"start": v(15, -104.25) * mm, "end": v(15, -92.25) * mm});
            skLineSegment(sketch, "E89.MirrorCS", {"start": v(0, -74.25) * mm, "end": v(0, -104.25) * mm, "construction": true});
            skCircle(sketch, "E90.MirrorC", {"center": v(0, -104.25) * mm, "radius": 6 * mm});
            skArc(sketch, "E91.MirrorCS", {"start": v(15, -104.25) * mm, "mid": v(0, -119.25) * mm, "end": v(-15, -104.25) * mm});
            skLineSegment(sketch, "E92.MirrorCS", {"start": v(15, -92.25) * mm, "end": v(33, -74.25) * mm});
            skLineSegment(sketch, "E93.MirrorCS", {"start": v(-15, -92.25) * mm, "end": v(-33, -74.25) * mm});
            skSolve(sketch);
        }
        {
            var Q0;
            Q0=makeQuery(id+"F16.imprint","IMPRINT",FACE,{"disambiguationData":[TD([[makeQuery(id+"F16.imprint","IMPRINT",EDGE,{"derivedFrom":sQuery(id+"F16.wireOp",EDGE,"E80")}),-1.0]])]});
            var Q1;
            Q1=makeQuery(id+"F16.imprint","IMPRINT",FACE,{"disambiguationData":[TD([[makeQuery(id+"F16.imprint","IMPRINT",EDGE,{"derivedFrom":sQuery(id+"F16.wireOp",EDGE,"E87.MirrorCS")}),-1.0]])]});
            var Q2;
            Q2=makeQuery(id+"F16.imprint","IMPRINT",FACE,{"disambiguationData":[TD([[makeQuery(id+"F16.imprint","IMPRINT",EDGE,{"derivedFrom":makeQuery(id+"F1.opExtrude","CAP_EDGE",EDGE,{"disambiguationData":[OSD([sQuery(id+"F0.wireOp",EDGE,"E1.left")])],"isStart":true})}),-1.0]])]});
            var Q3;
            Q3=makeQuery(id+"F2.opExtrude","CAP_FACE",FACE,{"disambiguationData":[OSD([sQuery(id+"F0.wireOp",EDGE,"E12"),sQuery(id+"F0.wireOp",EDGE,"E13"),sQuery(id+"F0.wireOp",EDGE,"E14"),sQuery(id+"F0.wireOp",EDGE,"E15"),sQuery(id+"F0.wireOp",EDGE,"E17.filletArc"),sQuery(id+"F0.wireOp",EDGE,"E18.filletArc"),sQuery(id+"F0.wireOp",EDGE,"E19.filletArc"),sQuery(id+"F0.wireOp",EDGE,"E20.filletArc"),sQuery(id+"F0.wireOp",EDGE,"E25.0"),sQuery(id+"F0.wireOp",EDGE,"E25.1"),sQuery(id+"F0.wireOp",EDGE,"E25.2"),sQuery(id+"F0.wireOp",EDGE,"E25.3"),sQuery(id+"F0.wireOp",EDGE,"E25.4"),sQuery(id+"F0.wireOp",EDGE,"E25.5"),sQuery(id+"F0.wireOp",EDGE,"E25.6"),sQuery(id+"F0.wireOp",EDGE,"E25.7")])],"isStart":false});
            extrude(context, id + "F17", {"entities" : qUnion([Q0, Q1, Q2]), "operationType" : NewBodyOperationType.ADD, "endBound" : BoundingType.UP_TO_SURFACE, "endBoundEntityFace" : qUnion([Q3]), "depth" : 25 * mm});
        }
    });
